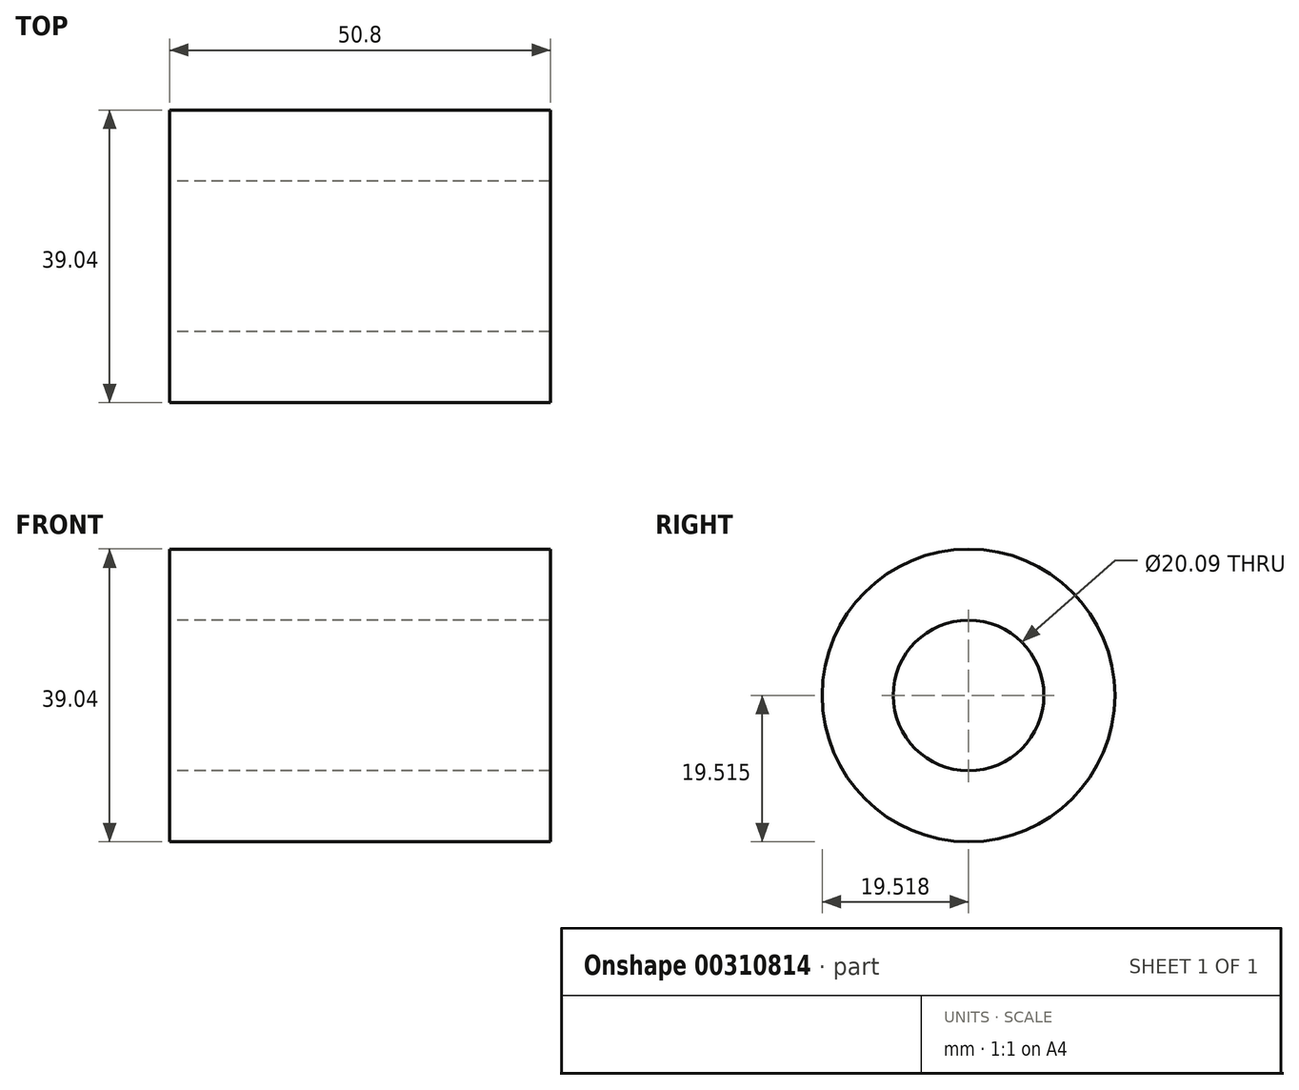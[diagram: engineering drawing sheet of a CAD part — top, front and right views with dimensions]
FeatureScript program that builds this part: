
annotation { "Feature Type Name" : "Feature", "Feature Type Description" : "" }
export const myFeature = defineFeature(function(context is Context, id is Id, definition is map)
    precondition{}
    {
        {
            var Q0;
            Q0=qCreatedBy(makeId("Right.planeOp"),FACE);
            var sketch = newSketch(context, id + "F0", { "sketchPlane" : qUnion([Q0])});
            skCircle(sketch, "E0", {"center": v(-27.82, 18.27) * mm, "radius": 19.52 * mm});
            skCircle(sketch, "E1", {"center": v(-27.82, 18.27) * mm, "radius": 10.05 * mm});
            skSolve(sketch);
        }
        {
            var Q0;
            Q0=makeQuery(id+"F0.imprint","IMPRINT",FACE,{"disambiguationData":[TD([[makeQuery(id+"F0.imprint","IMPRINT",EDGE,{"derivedFrom":sQuery(id+"F0.wireOp",EDGE,"E0")}),1.0]])]});
            extrude(context, id + "F1", {"entities" : qUnion([Q0]), "depth" : 25.4 * mm});
        }
        {
            var Q0;
            Q0=makeQuery(id+"F1.opExtrude","CAP_FACE",FACE,{"disambiguationData":[OSD([sQuery(id+"F0.wireOp",EDGE,"E0"),sQuery(id+"F0.wireOp",EDGE,"E1")])],"isStart":false});
            var sketch = newSketch(context, id + "F2", { "sketchPlane" : qUnion([Q0])});
            skSolve(sketch);
        }
        {
            var Q0;
            Q0=makeQuery(id+"F2.imprint","IMPRINT",FACE,{"disambiguationData":[TD([[makeQuery(id+"F2.imprint","IMPRINT",EDGE,{"derivedFrom":makeQuery(id+"F1.opExtrude","CAP_EDGE",EDGE,{"disambiguationData":[OSD([sQuery(id+"F0.wireOp",EDGE,"E0")])],"isStart":false})}),1.0]])]});
            var sketch = newSketch(context, id + "F3", { "sketchPlane" : qUnion([Q0])});
            skCircle(sketch, "E2", {"center": v(-44.26, 16.12) * mm, "radius": 2.2 * mm});
            skCircle(sketch, "E3", {"center": v(-43.38, 22.55) * mm, "radius": 2.04 * mm});
            skCircle(sketch, "E4", {"center": v(-41.1, 27.05) * mm, "radius": 1.67 * mm});
            skCircle(sketch, "E5", {"center": v(-36.86, 29.67) * mm, "radius": 1.89 * mm});
            skCircle(sketch, "E6", {"center": v(-31.57, 31.45) * mm, "radius": 1.74 * mm});
            skCircle(sketch, "E7", {"center": v(-23.64, 30.54) * mm, "radius": 2.24 * mm});
            skCircle(sketch, "E8", {"center": v(-14.48, 23.97) * mm, "radius": 2.39 * mm});
            skCircle(sketch, "E9", {"center": v(-13.6, 17.28) * mm, "radius": 2.2 * mm});
            skCircle(sketch, "E10", {"center": v(-17.12, 12.17) * mm, "radius": 2.12 * mm});
            skCircle(sketch, "E11", {"center": v(-19.77, 5.86) * mm, "radius": 2.75 * mm});
            skCircle(sketch, "E12", {"center": v(-27, 5.05) * mm, "radius": 2.6 * mm});
            skCircle(sketch, "E13", {"center": v(-36.86, 8.76) * mm, "radius": 2.64 * mm});
            skSolve(sketch);
        }
        {
            var Q0;
            Q0=makeQuery(id+"F3.imprint","IMPRINT",FACE,{"disambiguationData":[TD([[makeQuery(id+"F3.imprint","IMPRINT",EDGE,{"derivedFrom":sQuery(id+"F3.wireOp",EDGE,"E3")}),1.0]])]});
            var Q1;
            Q1=makeQuery(id+"F3.imprint","IMPRINT",FACE,{"disambiguationData":[TD([[makeQuery(id+"F3.imprint","IMPRINT",EDGE,{"derivedFrom":sQuery(id+"F3.wireOp",EDGE,"E4")}),1.0]])]});
            var Q2;
            Q2=makeQuery(id+"F2.imprint","IMPRINT",FACE,{"disambiguationData":[TD([[makeQuery(id+"F2.imprint","IMPRINT",EDGE,{"derivedFrom":makeQuery(id+"F1.opExtrude","CAP_EDGE",EDGE,{"disambiguationData":[OSD([sQuery(id+"F0.wireOp",EDGE,"E0")])],"isStart":false})}),1.0]])]});
            var Q3;
            Q3=makeQuery(id+"F3.imprint","IMPRINT",FACE,{"disambiguationData":[TD([[makeQuery(id+"F3.imprint","IMPRINT",EDGE,{"derivedFrom":sQuery(id+"F3.wireOp",EDGE,"E6")}),1.0]])]});
            extrude(context, id + "F4", {"entities" : qUnion([Q0, Q1, Q2, Q3]), "operationType" : NewBodyOperationType.ADD, "depth" : 25.4 * mm});
        }
    });
